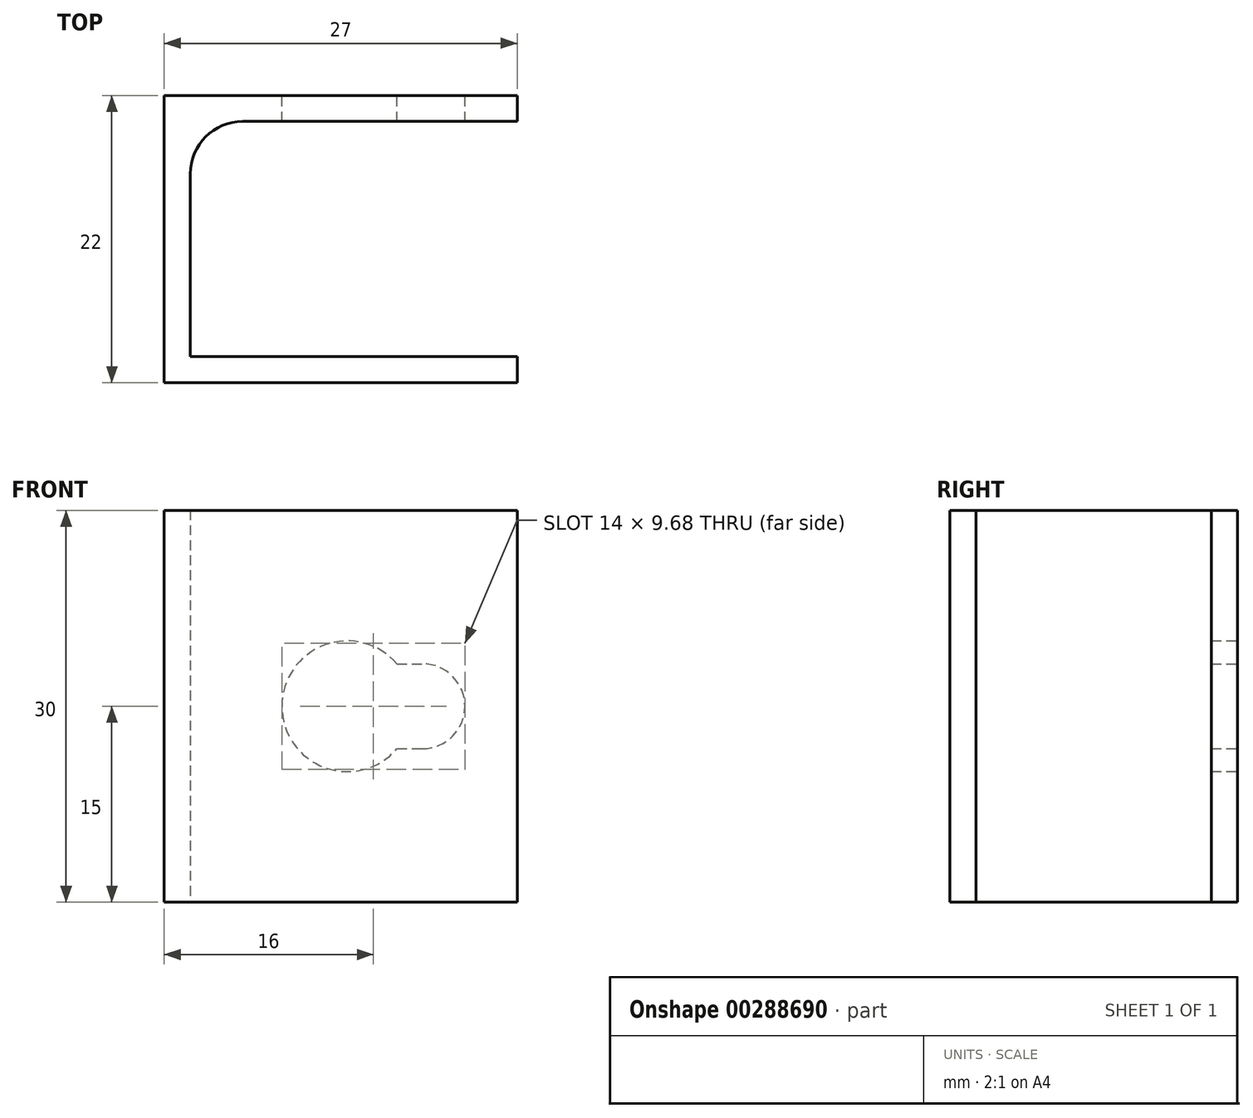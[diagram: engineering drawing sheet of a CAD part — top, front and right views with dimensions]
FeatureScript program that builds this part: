
annotation { "Feature Type Name" : "Feature", "Feature Type Description" : "" }
export const myFeature = defineFeature(function(context is Context, id is Id, definition is map)
    precondition{}
    {
        {
            var Q0;
            Q0=qCreatedBy(makeId("Top.planeOp"),FACE);
            var sketch = newSketch(context, id + "F0", { "sketchPlane" : qUnion([Q0])});
            skLineSegment(sketch, "E0.bottom", {"start": v(13.5, -11) * mm, "end": v(-13.5, -11) * mm});
            skLineSegment(sketch, "E0.top", {"start": v(13.5, 11) * mm, "end": v(-13.5, 11) * mm});
            skLineSegment(sketch, "E0.left", {"start": v(13.5, -11) * mm, "end": v(13.5, -9) * mm});
            skLineSegment(sketch, "E0.right", {"start": v(-13.5, -11) * mm, "end": v(-13.5, 11) * mm});
            skPoint(sketch, "E0.middle", {"position": v(0, 0) * mm});
            skLineSegment(sketch, "E1.bottom", {"start": v(13.5, 9) * mm, "end": v(-7.5, 9) * mm});
            skLineSegment(sketch, "E1.top", {"start": v(13.5, -9) * mm, "end": v(-11.5, -9) * mm});
            skLineSegment(sketch, "E1.right", {"start": v(-11.5, 5) * mm, "end": v(-11.5, -9) * mm});
            skLineSegment(sketch, "E2.trimOffspring", {"start": v(13.5, 9) * mm, "end": v(13.5, 11) * mm});
            skLineSegment(sketch, "E3", {"start": v(-11.5, 0) * mm, "end": v(-13.5, 0) * mm, "construction": true});
            skPoint(sketch, "E4.visualSharp", {"position": v(-11.5, 9) * mm});
            skArc(sketch, "E4.filletArc", {"start": v(-7.5, 9) * mm, "mid": v(-10.33, 7.83) * mm, "end": v(-11.5, 5) * mm});
            skSolve(sketch);
        }
        {
            var Q0;
            Q0=makeQuery(id+"F0.imprint","IMPRINT",FACE,{"disambiguationData":[TD([[makeQuery(id+"F0.imprint","IMPRINT",EDGE,{"derivedFrom":sQuery(id+"F0.wireOp",EDGE,"E0.bottom")}),-1.0]])]});
            extrude(context, id + "F1", {"entities" : qUnion([Q0]), "depth" : 30 * mm});
        }
        {
            var Q0;
            Q0=makeQuery(id+"F1.opExtrude","SWEPT_FACE",FACE,{"disambiguationData":[OSD([sQuery(id+"F0.wireOp",EDGE,"E0.top")])]});
            var sketch = newSketch(context, id + "F2", { "sketchPlane" : qUnion([Q0])});
            skArc(sketch, "E5", {"start": v(-4.3, 11.75) * mm, "mid": v(4.5, 15) * mm, "end": v(-4.3, 18.25) * mm});
            skPoint(sketch, "E5.centerSnap0", {"position": v(-13.5, 15) * mm});
            skLineSegment(sketch, "E6.bottom", {"start": v(-0.5, 11.75) * mm, "end": v(-9.5, 11.75) * mm});
            skLineSegment(sketch, "E6.top", {"start": v(-0.5, 18.25) * mm, "end": v(-9.5, 18.25) * mm});
            skLineSegment(sketch, "E6.left", {"start": v(-0.5, 11.75) * mm, "end": v(-0.5, 18.25) * mm});
            skLineSegment(sketch, "E6.right", {"start": v(-9.5, 11.75) * mm, "end": v(-9.5, 18.25) * mm, "construction": true});
            skArc(sketch, "E7", {"start": v(-6.25, 18.25) * mm, "mid": v(-9.5, 15) * mm, "end": v(-6.25, 11.75) * mm});
            skPoint(sketch, "E7.centerSnap0", {"position": v(-9.5, 15) * mm});
            skSolve(sketch);
        }
        {
            var Q0;
            {var subQ4=sQuery(id+"F2.wireOp",EDGE,"E6.left");Q0=makeQuery(id+"F2.imprint","IMPRINT",FACE,{"disambiguationData":[TD([[makeQuery(id+"F2.imprint","IMPRINT",EDGE,{"derivedFrom":subQ4}),1.0]])]});}
            var Q1;
            {var subQ0=sQuery(id+"F2.wireOp",EDGE,"E5");Q1=makeQuery(id+"F2.imprint","IMPRINT",FACE,{"disambiguationData":[TD([[makeQuery(id+"F2.imprint","IMPRINT",EDGE,{"derivedFrom":subQ0}),1.0]])]});}
            extrude(context, id + "F3", {"entities" : qUnion([Q0, Q1]), "operationType" : NewBodyOperationType.REMOVE, "endBound" : BoundingType.UP_TO_NEXT, "oppositeDirection" : true, "depth" : 25 * mm});
        }
    });
